FCSTD DOCUMENT  (FreeCAD 0.21R33771 (Git))
Label: tc2-mic-pcb
License: All rights reserved
LicenseURL: https://en.wikipedia.org/wiki/All_rights_reserved
objects: Sketcher::SketchObject×2
note: 2 computed .brp shape members not serialized (recipe doc carries the construction recipe); baked Part::Feature solids carry a one-line shape summary decoded from their .brp

FEATURE [Sketcher::SketchObject] Sketch  label="boarder"
  FullyConstrained = true
  MapMode = 5
  Placement = pos=(-5,4,0) rot=(0,0,1;0rad)
  sketch-geometry (11):
    g0: LineSegment StartX=39 StartY=-4 StartZ=0 EndX=39 EndY=-14 EndZ=0
    g1: LineSegment StartX=38 StartY=-15 StartZ=0 EndX=1 EndY=-15 EndZ=0
    g2: LineSegment StartX=-3e-16 StartY=-14 StartZ=0 EndX=-3e-16 EndY=-5.75 EndZ=0
    g3: ArcOfCircle CenterX=0 CenterY=-4 CenterZ=0 NormalX=0 NormalY=0 NormalZ=1 AngleXU=0 Radius=1.75 StartAngle=4.71239 EndAngle=7.85398
    g4: ArcOfCircle CenterX=35 CenterY=-4 CenterZ=0 NormalX=0 NormalY=0 NormalZ=1 AngleXU=0 Radius=4 StartAngle=0 EndAngle=1.5708
    g5: ArcOfCircle CenterX=38 CenterY=-14 CenterZ=0 NormalX=0 NormalY=0 NormalZ=1 AngleXU=0 Radius=1 StartAngle=4.71239 EndAngle=6.28319
    g6: ArcOfCircle CenterX=1 CenterY=-14 CenterZ=0 NormalX=0 NormalY=0 NormalZ=1 AngleXU=0 Radius=1 StartAngle=3.14159 EndAngle=4.71239
    g7: LineSegment StartX=5e-16 StartY=-2.25 StartZ=0 EndX=0 EndY=-1 EndZ=0
    g8: LineSegment StartX=1 StartY=0 StartZ=0 EndX=35 EndY=0 EndZ=0
    g9: ArcOfCircle CenterX=1 CenterY=-1 CenterZ=0 NormalX=0 NormalY=0 NormalZ=1 AngleXU=0 Radius=1 StartAngle=1.5708 EndAngle=3.14159
    g10: Circle CenterX=35 CenterY=-4 CenterZ=0 NormalX=0 NormalY=0 NormalZ=1 AngleXU=0 Radius=1.75
  constraints (29):
    c: Vertical(g0)
    c: Horizontal(g1)
    c: PointOnObject(g2,g-2)
    c: PointOnObject(g3,g-2)
    c: PointOnObject(g3,g-2)
    c: Coincident(g3,g2)
    c: Radius(g3) = 1.75
    c: DistanceY(g3,g-1) = 4
    c: Tangent(g0,g4) = 1.5708
    c: Tangent(g0,g5) = 1.5708
    c: Tangent(g1,g5) = 1.5708
    c: Tangent(g1,g6) = 1.5708
    c: Tangent(g2,g6) = 1.5708
    c: Coincident(g7,g3)
    c: PointOnObject(g7,g-2)
    c: PointOnObject(g8,g-1)
    c: Horizontal(g8)
    c: Tangent(g9,g7) = 1.5708
    c: Tangent(g9,g8) = 1.5708
    c: Equal(g9,g6)
    c: Equal(g9,g5)
    c: Radius(g9) = 1
    c: Vertical(g2)
    c: DistanceY(g1,g8) = 15
    c: DistanceX(g7,g0) = 39
    c: Radius(g4) = 4
    c: Tangent(g8,g4) = 1.5708
    c: Coincident(g10,g4)
    c: Diameter(g10) = 3.5
FEATURE [Sketcher::SketchObject] Sketch001  label="features"
  FullyConstrained = true
  MapMode = 5
  Placement = pos=(-5,4,0) rot=(0,0,1;0rad)
  sketch-geometry (3):
    g0: Circle CenterX=5 CenterY=-4 CenterZ=0 NormalX=0 NormalY=0 NormalZ=1 AngleXU=0 Radius=2
    g1: Circle CenterX=13 CenterY=-4 CenterZ=0 NormalX=0 NormalY=0 NormalZ=1 AngleXU=0 Radius=1
    g2: Circle CenterX=28 CenterY=-4 CenterZ=0 NormalX=0 NormalY=0 NormalZ=1 AngleXU=0 Radius=2
  constraints (9):
    c: Equal(g0,g2)
    c: Diameter(g0) = 4
    c: Horizontal(g0,g1)
    c: Horizontal(g1,g2)
    c: DistanceY(g0,g-1) = 4
    c: DistanceX(g-1,g0) = 5
    c: DistanceX(g-1,g1) = 13
    c: DistanceX(g-1,g2) = 28
    c: Diameter(g1) = 2
